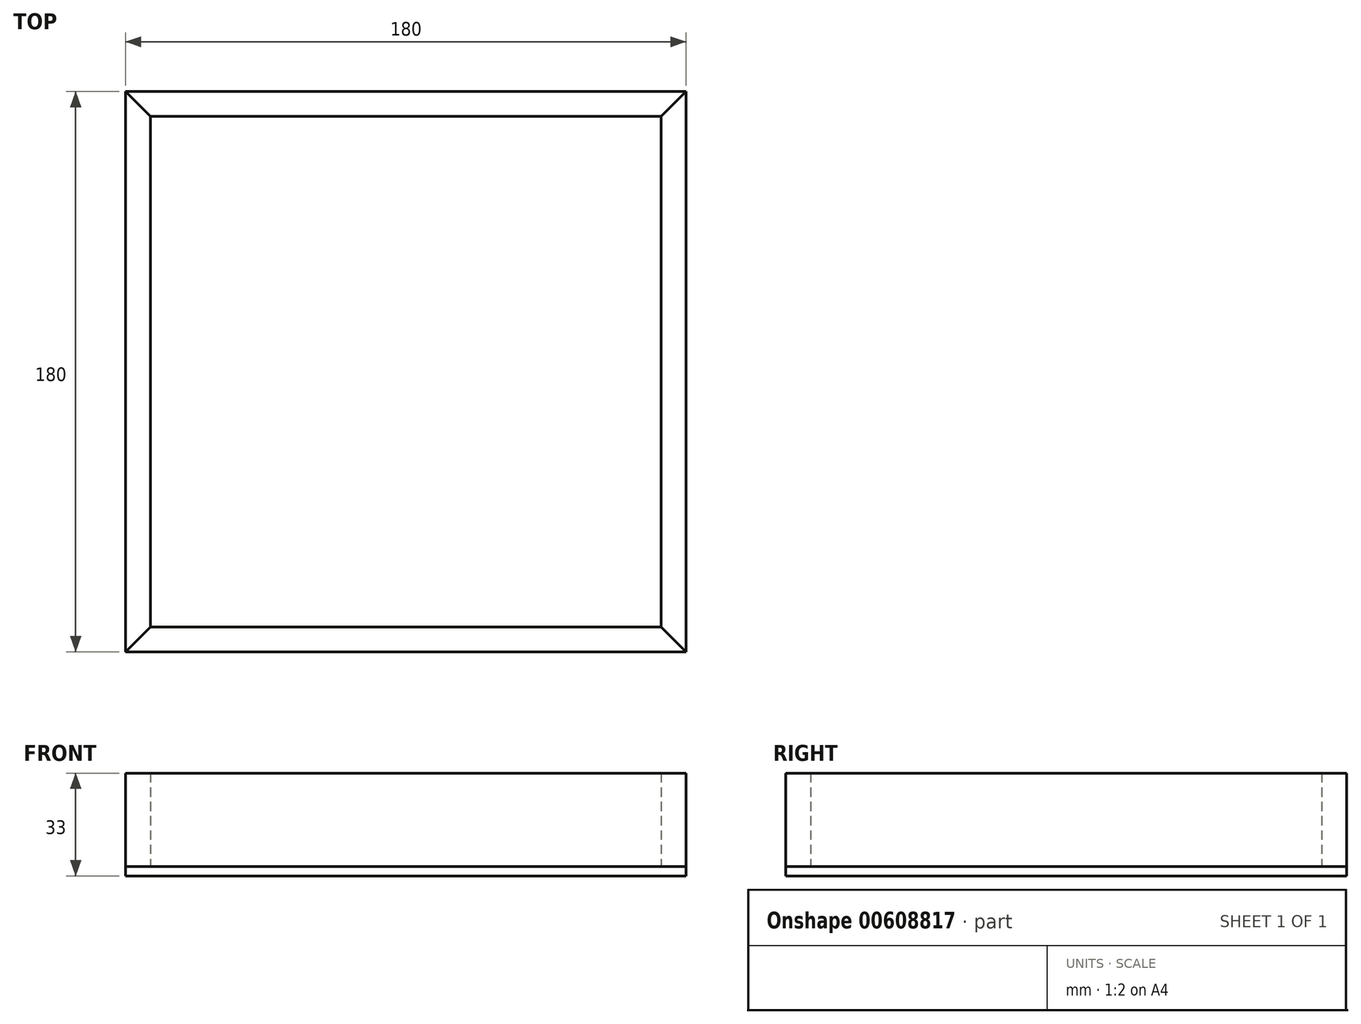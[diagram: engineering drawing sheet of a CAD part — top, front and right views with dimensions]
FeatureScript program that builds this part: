
annotation { "Feature Type Name" : "Feature", "Feature Type Description" : "" }
export const myFeature = defineFeature(function(context is Context, id is Id, definition is map)
    precondition{}
    {
        {
            var Q0;
            Q0=qCreatedBy(makeId("Top.planeOp"),FACE);
            var sketch = newSketch(context, id + "F0", { "sketchPlane" : qUnion([Q0])});
            skLineSegment(sketch, "E0.bottom", {"start": v(0, 0) * mm, "end": v(180, 0) * mm});
            skLineSegment(sketch, "E0.top", {"start": v(0, 180) * mm, "end": v(180, 180) * mm});
            skLineSegment(sketch, "E0.left", {"start": v(0, 0) * mm, "end": v(0, 180) * mm});
            skLineSegment(sketch, "E0.right", {"start": v(180, 0) * mm, "end": v(180, 180) * mm});
            skSolve(sketch);
        }
        {
            var Q0;
            Q0=makeQuery(id+"F0.imprint","IMPRINT",FACE,{"disambiguationData":[TD([[makeQuery(id+"F0.imprint","IMPRINT",EDGE,{"derivedFrom":sQuery(id+"F0.wireOp",EDGE,"E0.bottom")}),1.0]])]});
            extrude(context, id + "F1", {"entities" : qUnion([Q0]), "depth" : 3 * mm, "offsetDistance" : 25 * mm});
        }
        {
            var Q0;
            Q0=makeQuery(id+"F1.opExtrude","CAP_FACE",FACE,{"disambiguationData":[OSD([sQuery(id+"F0.wireOp",EDGE,"E0.bottom"),sQuery(id+"F0.wireOp",EDGE,"E0.top"),sQuery(id+"F0.wireOp",EDGE,"E0.left"),sQuery(id+"F0.wireOp",EDGE,"E0.right")])],"isStart":false});
            var sketch = newSketch(context, id + "F2", { "sketchPlane" : qUnion([Q0])});
            skLineSegment(sketch, "E1.0", {"start": v(8, 172) * mm, "end": v(172, 172) * mm});
            skLineSegment(sketch, "E1.1", {"start": v(8, 8) * mm, "end": v(8, 172) * mm});
            skLineSegment(sketch, "E1.2", {"start": v(8, 8) * mm, "end": v(172, 8) * mm});
            skLineSegment(sketch, "E1.3", {"start": v(172, 8) * mm, "end": v(172, 172) * mm});
            skLineSegment(sketch, "E2", {"start": v(8, 172) * mm, "end": v(0, 180) * mm});
            skLineSegment(sketch, "E3", {"start": v(172, 172) * mm, "end": v(180, 180) * mm});
            skLineSegment(sketch, "E4", {"start": v(0, 0) * mm, "end": v(8, 8) * mm});
            skLineSegment(sketch, "E5", {"start": v(172, 8) * mm, "end": v(180, 0) * mm});
            skSolve(sketch);
        }
        {
            var Q0;
            Q0=makeQuery(id+"F2.imprint","IMPRINT",FACE,{"disambiguationData":[TD([[makeQuery(id+"F2.imprint","IMPRINT",EDGE,{"derivedFrom":sQuery(id+"F2.wireOp",EDGE,"E1.0")}),1.0]])]});
            extrude(context, id + "F3", {"entities" : qUnion([Q0]), "depth" : 30 * mm, "offsetDistance" : 25 * mm});
        }
        {
            var Q0;
            Q0=makeQuery(id+"F2.imprint","IMPRINT",FACE,{"disambiguationData":[TD([[makeQuery(id+"F2.imprint","IMPRINT",EDGE,{"derivedFrom":sQuery(id+"F2.wireOp",EDGE,"E1.3")}),-1.0]])]});
            var Q1;
            Q1=makeQuery(id+"F3.opExtrude","SWEPT_BODY",BODY,{"disambiguationData":[OSD([sQuery(id+"F0.wireOp",EDGE,"E0.top"),sQuery(id+"F2.wireOp",EDGE,"E1.0"),sQuery(id+"F2.wireOp",EDGE,"E2"),sQuery(id+"F2.wireOp",EDGE,"E3")])]});
            var Q2;
            Q2=makeQuery(id+"F3.opExtrude","CAP_VERTEX",VERTEX,{"disambiguationData":[OSD([sQuery(id+"F2.wireOp",EDGE,"E1.0"),sQuery(id+"F2.wireOp",EDGE,"E1.3"),sQuery(id+"F2.wireOp",EDGE,"E3")])],"isStart":false});
            extrude(context, id + "F4", {"entities" : qUnion([Q0]), "endBound" : BoundingType.UP_TO_VERTEX, "depth" : 25 * mm, "endBoundEntityBody" : qUnion([Q1]), "endBoundEntityVertex" : qUnion([Q2]), "offsetDistance" : 25 * mm});
        }
        {
            var Q0;
            Q0=makeQuery(id+"F2.imprint","IMPRINT",FACE,{"disambiguationData":[TD([[makeQuery(id+"F2.imprint","IMPRINT",EDGE,{"derivedFrom":sQuery(id+"F2.wireOp",EDGE,"E1.2")}),-1.0]])]});
            var Q1;
            Q1=makeQuery(id+"F4.opExtrude","CAP_VERTEX",VERTEX,{"disambiguationData":[OSD([sQuery(id+"F2.wireOp",EDGE,"E1.2"),sQuery(id+"F2.wireOp",EDGE,"E1.3"),sQuery(id+"F2.wireOp",EDGE,"E5"),dummyQuery(id+"F4.vertexPlane.planeOp",FACE)])],"isStart":false});
            extrude(context, id + "F5", {"entities" : qUnion([Q0]), "endBound" : BoundingType.UP_TO_VERTEX, "depth" : 25 * mm, "endBoundEntityVertex" : qUnion([Q1]), "offsetDistance" : 25 * mm});
        }
        {
            var Q0;
            Q0=makeQuery(id+"F2.imprint","IMPRINT",FACE,{"disambiguationData":[TD([[makeQuery(id+"F2.imprint","IMPRINT",EDGE,{"derivedFrom":sQuery(id+"F2.wireOp",EDGE,"E1.1")}),1.0]])]});
            var Q1;
            Q1=makeQuery(id+"F3.opExtrude","CAP_VERTEX",VERTEX,{"disambiguationData":[OSD([sQuery(id+"F0.wireOp",EDGE,"E0.top"),sQuery(id+"F0.wireOp",EDGE,"E0.left"),sQuery(id+"F2.wireOp",EDGE,"E2")])],"isStart":false});
            extrude(context, id + "F6", {"entities" : qUnion([Q0]), "endBound" : BoundingType.UP_TO_VERTEX, "depth" : 25 * mm, "endBoundEntityVertex" : qUnion([Q1]), "offsetDistance" : 25 * mm});
        }
    });
